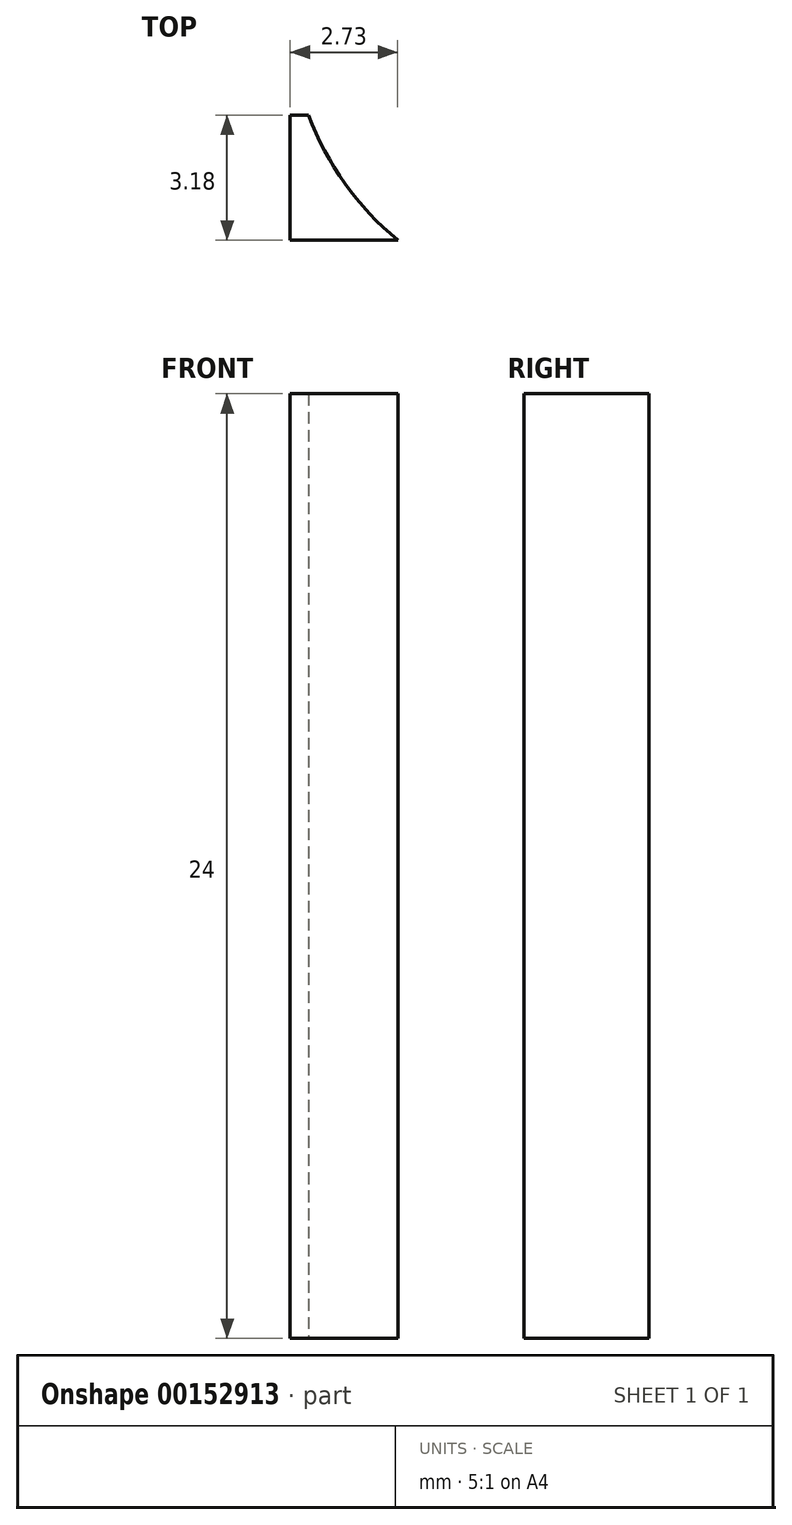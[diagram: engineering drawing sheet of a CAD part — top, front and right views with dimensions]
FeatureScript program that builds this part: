
annotation { "Feature Type Name" : "Feature", "Feature Type Description" : "" }
export const myFeature = defineFeature(function(context is Context, id is Id, definition is map)
    precondition{}
    {
        {
            var Q0;
            Q0=qCreatedBy(makeId("Top.planeOp"),FACE);
            var sketch = newSketch(context, id + "F0", { "sketchPlane" : qUnion([Q0])});
            skLineSegment(sketch, "E0.bottom", {"start": v(0, 0) * mm, "end": v(-0.47, 0) * mm});
            skLineSegment(sketch, "E0.top", {"start": v(2.26, -3.18) * mm, "end": v(-0.47, -3.18) * mm});
            skLineSegment(sketch, "E0.right", {"start": v(-0.47, 0) * mm, "end": v(-0.47, -3.18) * mm});
            skArc(sketch, "E1", {"start": v(0, 0) * mm, "mid": v(0.92, -1.74) * mm, "end": v(2.26, -3.18) * mm});
            skLineSegment(sketch, "E2", {"start": v(2.26, -3.18) * mm, "end": v(2.26, -4.88) * mm, "construction": true});
            skLineSegment(sketch, "E3", {"start": v(2.26, -4.88) * mm, "end": v(7.03, -4.88) * mm, "construction": true});
            skLineSegment(sketch, "E4", {"start": v(7.03, 2.62) * mm, "end": v(7.03, -4.88) * mm, "construction": true});
            skSolve(sketch);
        }
        {
            var Q0;
            Q0=qSketchRegion(id+"F0",true);
            extrude(context, id + "F1", {"entities" : qUnion([Q0]), "depth" : 24 * mm});
        }
    });
